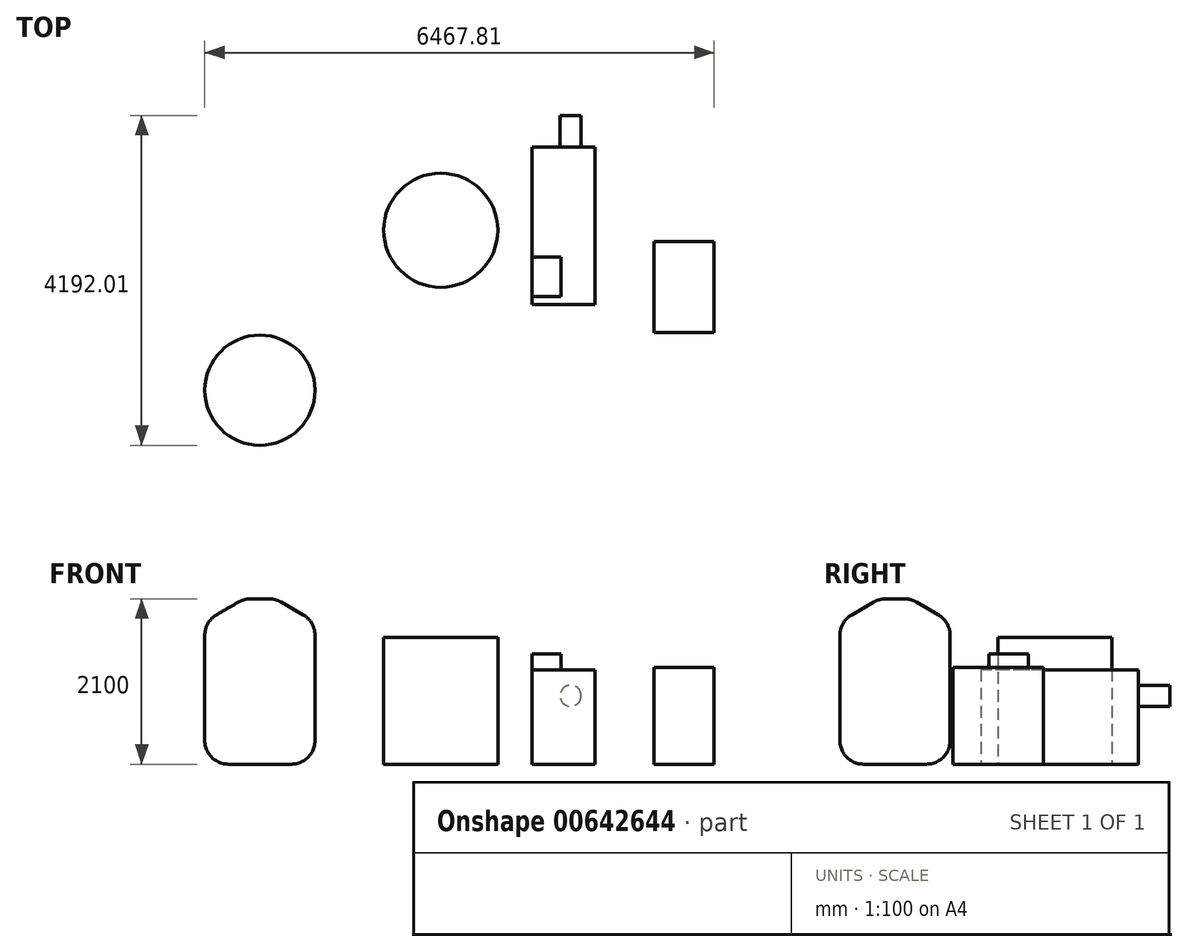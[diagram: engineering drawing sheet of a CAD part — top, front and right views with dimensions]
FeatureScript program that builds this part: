
annotation { "Feature Type Name" : "Feature", "Feature Type Description" : "" }
export const myFeature = defineFeature(function(context is Context, id is Id, definition is map)
    precondition{}
    {
        {
            var Q0;
            Q0=qCreatedBy(makeId("Top.planeOp"),FACE);
            var sketch = newSketch(context, id + "F0", { "sketchPlane" : qUnion([Q0])});
            skLineSegment(sketch, "E0.bottom", {"start": v(-411.47, -694.24) * mm, "end": v(348.53, -694.24) * mm});
            skLineSegment(sketch, "E0.top", {"start": v(-411.47, 455.76) * mm, "end": v(348.53, 455.76) * mm});
            skLineSegment(sketch, "E0.left", {"start": v(-411.47, -694.24) * mm, "end": v(-411.47, 455.76) * mm});
            skLineSegment(sketch, "E0.right", {"start": v(348.53, -694.24) * mm, "end": v(348.53, 455.76) * mm});
            skSolve(sketch);
        }
        {
            var Q0;
            Q0 = qSketchRegion(id + "F0", true);
            extrude(context, id + "F1", {"entities" : qUnion([Q0]), "depth" : 1230 * mm, "offsetDistance" : 25 * mm});
        }
        {
            var Q0;
            Q0=qCreatedBy(makeId("Top.planeOp"),FACE);
            var sketch = newSketch(context, id + "F2", { "sketchPlane" : qUnion([Q0])});
            skCircle(sketch, "E1", {"center": v(-3121.8, 602.2) * mm, "radius": 725 * mm});
            skSolve(sketch);
        }
        {
            var Q0;
            Q0=makeQuery(id+"F2.imprint","IMPRINT",FACE,{"disambiguationData":[TD([[makeQuery(id+"F2.imprint","IMPRINT",EDGE,{"derivedFrom":sQuery(id+"F2.wireOp",EDGE,"E1")}),1.0]])]});
            extrude(context, id + "F3", {"entities" : qUnion([Q0]), "depth" : 1610 * mm, "offsetDistance" : 25 * mm});
        }
        {
            var Q0;
            Q0=qCreatedBy(makeId("Top.planeOp"),FACE);
            var sketch = newSketch(context, id + "F4", { "sketchPlane" : qUnion([Q0])});
            skLineSegment(sketch, "E2.bottom", {"start": v(-1964.82, 1661.78) * mm, "end": v(-1164.82, 1661.78) * mm});
            skLineSegment(sketch, "E2.top", {"start": v(-1964.82, -338.22) * mm, "end": v(-1164.82, -338.22) * mm});
            skLineSegment(sketch, "E2.left", {"start": v(-1964.82, 1661.78) * mm, "end": v(-1964.82, -338.22) * mm});
            skLineSegment(sketch, "E2.right", {"start": v(-1164.82, 1661.78) * mm, "end": v(-1164.82, -338.22) * mm});
            skSolve(sketch);
        }
        {
            var Q0;
            Q0 = qSketchRegion(id + "F4", true);
            extrude(context, id + "F5", {"entities" : qUnion([Q0]), "depth" : 1200 * mm, "offsetDistance" : 25 * mm});
        }
        {
            var Q0;
            Q0=makeQuery(id+"F5.opExtrude","CAP_FACE",FACE,{"disambiguationData":[OSD([sQuery(id+"F4.wireOp",EDGE,"E2.bottom"),sQuery(id+"F4.wireOp",EDGE,"E2.top"),sQuery(id+"F4.wireOp",EDGE,"E2.left"),sQuery(id+"F4.wireOp",EDGE,"E2.right")])],"isStart":false});
            var sketch = newSketch(context, id + "F6", { "sketchPlane" : qUnion([Q0])});
            skLineSegment(sketch, "E3.bottom", {"start": v(-1594.82, 261.78) * mm, "end": v(-1964.82, 261.78) * mm});
            skLineSegment(sketch, "E3.top", {"start": v(-1594.82, -238.22) * mm, "end": v(-1964.82, -238.22) * mm});
            skLineSegment(sketch, "E3.left", {"start": v(-1594.82, 261.78) * mm, "end": v(-1594.82, -238.22) * mm});
            skLineSegment(sketch, "E3.right", {"start": v(-1964.82, 261.78) * mm, "end": v(-1964.82, -238.22) * mm});
            skSolve(sketch);
        }
        {
            var Q0;
            Q0 = qSketchRegion(id + "F6", true);
            extrude(context, id + "F7", {"entities" : qUnion([Q0]), "operationType" : NewBodyOperationType.ADD, "depth" : 200 * mm, "offsetDistance" : 25 * mm});
        }
        {
            var Q0;
            Q0=qCreatedBy(makeId("Top.planeOp"),FACE);
            var sketch = newSketch(context, id + "F8", { "sketchPlane" : qUnion([Q0])});
            skCircle(sketch, "E4", {"center": v(-5419.28, -1430.23) * mm, "radius": 700 * mm});
            skSolve(sketch);
        }
        {
            var Q0;
            Q0 = qSketchRegion(id + "F8", true);
            extrude(context, id + "F9", {"entities" : qUnion([Q0]), "depth" : 2100 * mm, "offsetDistance" : 25 * mm});
        }
        {
            var Q0;
            Q0=makeQuery(id+"F9.opExtrude","CAP_EDGE",EDGE,{"disambiguationData":[OSD([sQuery(id+"F8.wireOp",EDGE,"E4")])],"isStart":true});
            fillet(context, id + "F10", {"entities" : qUnion([Q0]), "radius" : 300 * mm, "tangentPropagation" : true, "allowEdgeOverflow" : false});
        }
        {
            var Q0;
            Q0=makeQuery(id+"F9.opExtrude","CAP_EDGE",EDGE,{"disambiguationData":[OSD([sQuery(id+"F8.wireOp",EDGE,"E4")])],"isStart":false});
            chamfer(context, id + "F11", {"entities" : qUnion([Q0]), "chamferType" : ChamferType.OFFSET_ANGLE, "width" : 500 * mm, "oppositeDirection" : false, "angle" : 30 * degree, "tangentPropagation" : true});
        }
        {
            var Q0;
            {var subQ0=sQuery(id+"F8.wireOp",EDGE,"E4");Q0=makeQuery(id+"F11.opChamfer","BLEND_EDGE",EDGE,{"blendedFrom":[makeQuery(id+"F9.opExtrude","CAP_EDGE",EDGE,{"disambiguationData":[OSD([subQ0])],"isStart":false}),makeQuery(id+"F9.opExtrude","SWEPT_FACE",FACE,{"disambiguationData":[OSD([subQ0])]})],"blendedInto":[makeQuery(id+"F9.opExtrude","SWEPT_FACE",FACE,{"disambiguationData":[OSD([subQ0])]})]});}
            var Q1;
            {var subQ0=sQuery(id+"F8.wireOp",EDGE,"E4");Q1=makeQuery(id+"F11.opChamfer","BLEND_EDGE",EDGE,{"blendedFrom":[makeQuery(id+"F9.opExtrude","CAP_EDGE",EDGE,{"disambiguationData":[OSD([subQ0])],"isStart":false}),makeQuery(id+"F9.opExtrude","CAP_FACE",FACE,{"disambiguationData":[OSD([subQ0])],"isStart":false})],"blendedInto":[makeQuery(id+"F9.opExtrude","CAP_FACE",FACE,{"disambiguationData":[OSD([subQ0])],"isStart":false})]});}
            fillet(context, id + "F12", {"entities" : qUnion([Q0, Q1]), "radius" : 300 * mm, "tangentPropagation" : true, "allowEdgeOverflow" : false});
        }
        {
            var Q0;
            Q0=makeQuery(id+"F5.opExtrude","SWEPT_FACE",FACE,{"disambiguationData":[OSD([sQuery(id+"F4.wireOp",EDGE,"E2.bottom")])]});
            var sketch = newSketch(context, id + "F13", { "sketchPlane" : qUnion([Q0])});
            skCircle(sketch, "E5", {"center": v(1471.76, 867.94) * mm, "radius": 134.84 * mm});
            skSolve(sketch);
        }
        {
            var Q0;
            Q0 = qSketchRegion(id + "F13", true);
            extrude(context, id + "F14", {"entities" : qUnion([Q0]), "operationType" : NewBodyOperationType.ADD, "depth" : 400 * mm, "offsetDistance" : 25 * mm});
        }
    });
